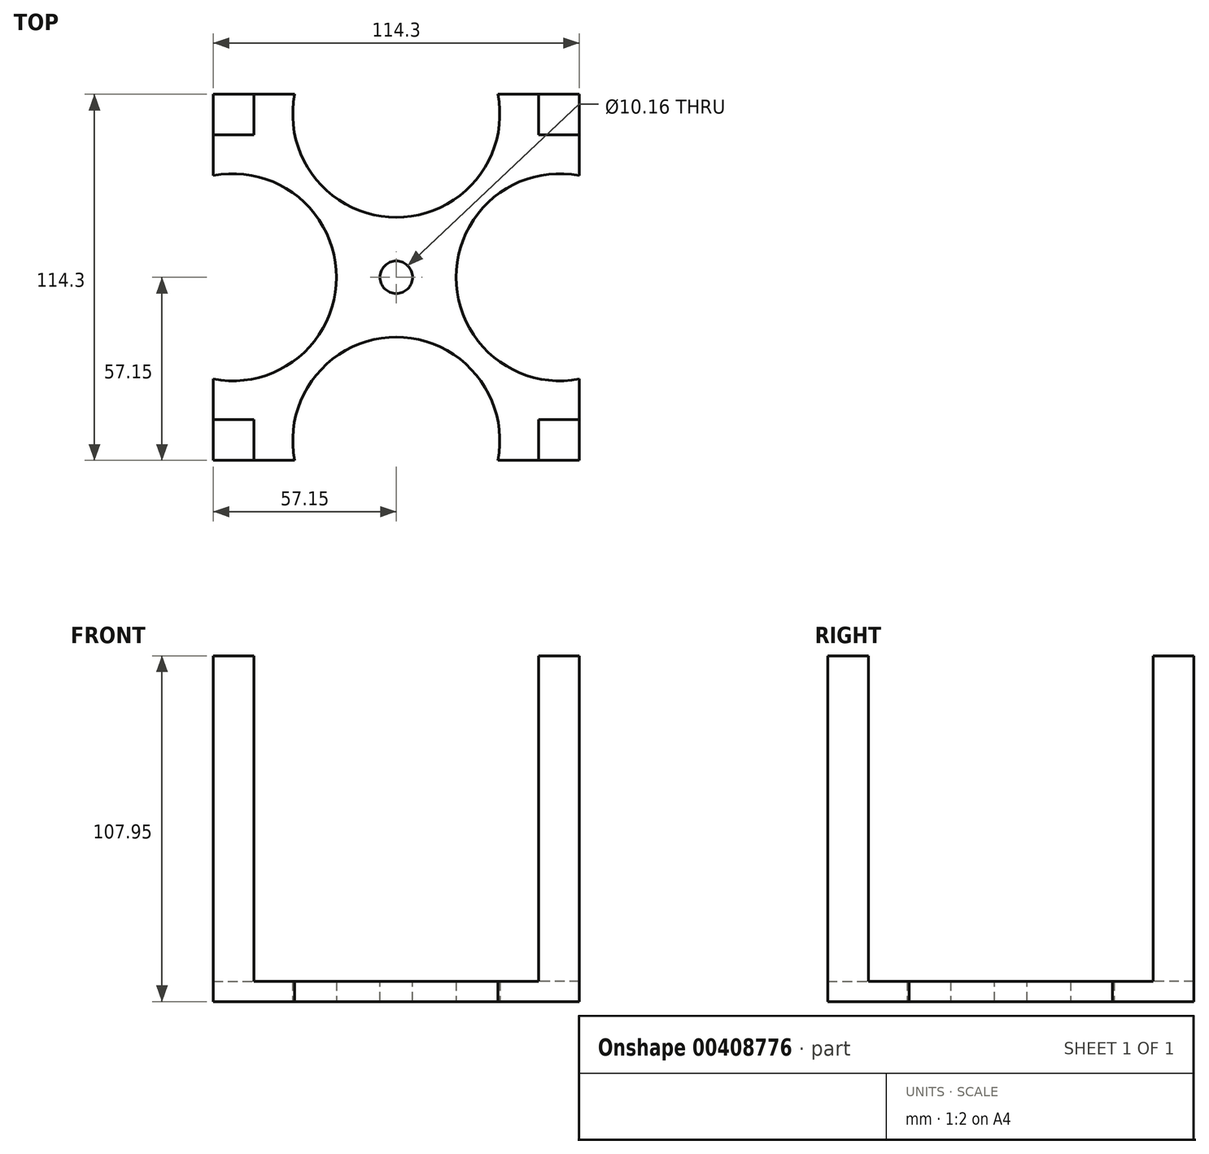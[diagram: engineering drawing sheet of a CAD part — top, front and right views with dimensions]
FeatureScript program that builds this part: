
annotation { "Feature Type Name" : "Feature", "Feature Type Description" : "" }
export const myFeature = defineFeature(function(context is Context, id is Id, definition is map)
    precondition{}
    {
        {
            var Q0;
            Q0=qCreatedBy(makeId("Top.planeOp"),FACE);
            var sketch = newSketch(context, id + "F0", { "sketchPlane" : qUnion([Q0])});
            skLineSegment(sketch, "E0.bottom", {"start": v(57.15, -57.15) * mm, "end": v(-57.15, -57.15) * mm});
            skLineSegment(sketch, "E0.top", {"start": v(57.15, 57.15) * mm, "end": v(-57.15, 57.15) * mm});
            skLineSegment(sketch, "E0.left", {"start": v(57.15, -57.15) * mm, "end": v(57.15, 57.15) * mm});
            skLineSegment(sketch, "E0.right", {"start": v(-57.15, -57.15) * mm, "end": v(-57.15, 57.15) * mm});
            skPoint(sketch, "E0.middle", {"position": v(0, 0) * mm});
            skSolve(sketch);
        }
        {
            var Q0;
            Q0 = qSketchRegion(id + "F0", true);
            extrude(context, id + "F1", {"entities" : qUnion([Q0]), "depth" : 6.35 * mm});
        }
        {
            var Q0;
            Q0=makeQuery(id+"F1.opExtrude","CAP_FACE",FACE,{"disambiguationData":[OSD([sQuery(id+"F0.wireOp",EDGE,"E0.bottom"),sQuery(id+"F0.wireOp",EDGE,"E0.top"),sQuery(id+"F0.wireOp",EDGE,"E0.left"),sQuery(id+"F0.wireOp",EDGE,"E0.right")])],"isStart":false});
            var sketch = newSketch(context, id + "F2", { "sketchPlane" : qUnion([Q0])});
            skLineSegment(sketch, "E1.bottom", {"start": v(57.15, 57.15) * mm, "end": v(44.45, 57.15) * mm});
            skLineSegment(sketch, "E1.top", {"start": v(57.15, 44.45) * mm, "end": v(44.45, 44.45) * mm});
            skLineSegment(sketch, "E1.left", {"start": v(57.15, 57.15) * mm, "end": v(57.15, 44.45) * mm});
            skLineSegment(sketch, "E1.right", {"start": v(44.45, 57.15) * mm, "end": v(44.45, 44.45) * mm});
            skLineSegment(sketch, "E2.1.0", {"start": v(-57.15, 44.45) * mm, "end": v(-44.45, 44.45) * mm});
            skLineSegment(sketch, "E2.1.1", {"start": v(-44.45, 57.15) * mm, "end": v(-44.45, 44.45) * mm});
            skLineSegment(sketch, "E2.1.2", {"start": v(-57.15, 57.15) * mm, "end": v(-44.45, 57.15) * mm});
            skLineSegment(sketch, "E2.1.3", {"start": v(-57.15, 57.15) * mm, "end": v(-57.15, 44.45) * mm});
            skLineSegment(sketch, "E2.2.0", {"start": v(-44.45, -57.15) * mm, "end": v(-44.45, -44.45) * mm});
            skLineSegment(sketch, "E2.2.1", {"start": v(-57.15, -44.45) * mm, "end": v(-44.45, -44.45) * mm});
            skLineSegment(sketch, "E2.2.2", {"start": v(-57.15, -57.15) * mm, "end": v(-57.15, -44.45) * mm});
            skLineSegment(sketch, "E2.2.3", {"start": v(-57.15, -57.15) * mm, "end": v(-44.45, -57.15) * mm});
            skLineSegment(sketch, "E2.3.0", {"start": v(57.15, -44.45) * mm, "end": v(44.45, -44.45) * mm});
            skLineSegment(sketch, "E2.3.1", {"start": v(44.45, -57.15) * mm, "end": v(44.45, -44.45) * mm});
            skLineSegment(sketch, "E2.3.2", {"start": v(57.15, -57.15) * mm, "end": v(44.45, -57.15) * mm});
            skLineSegment(sketch, "E2.3.3", {"start": v(57.15, -57.15) * mm, "end": v(57.15, -44.45) * mm});
            skPoint(sketch, "E2.center", {"position": v(0, 0) * mm});
            skSolve(sketch);
        }
        {
            var Q0;
            Q0=makeQuery(id+"F2.imprint","IMPRINT",FACE,{"disambiguationData":[TD([[makeQuery(id+"F2.imprint","IMPRINT",EDGE,{"derivedFrom":makeQuery(id+"F1.opExtrude","CAP_EDGE",EDGE,{"disambiguationData":[OSD([sQuery(id+"F0.wireOp",EDGE,"E0.bottom")])],"isStart":false})}),-1.0]])]});
            var sketch = newSketch(context, id + "F3", { "sketchPlane" : qUnion([Q0])});
            skCircle(sketch, "E3", {"center": v(0, 0) * mm, "radius": 5.08 * mm});
            skSolve(sketch);
        }
        {
            var Q0;
            Q0 = qSketchRegion(id + "F3", true);
            extrude(context, id + "F4", {"entities" : qUnion([Q0]), "operationType" : NewBodyOperationType.REMOVE, "oppositeDirection" : true, "depth" : 25.4 * mm});
        }
        {
            var Q0;
            Q0 = qSketchRegion(id + "F2", true);
            extrude(context, id + "F5", {"entities" : qUnion([Q0]), "operationType" : NewBodyOperationType.ADD, "depth" : 101.6 * mm});
        }
        {
            var Q0;
            Q0=makeQuery(id+"F1.opExtrude","CAP_FACE",FACE,{"disambiguationData":[OSD([sQuery(id+"F0.wireOp",EDGE,"E0.bottom"),sQuery(id+"F0.wireOp",EDGE,"E0.top"),sQuery(id+"F0.wireOp",EDGE,"E0.left"),sQuery(id+"F0.wireOp",EDGE,"E0.right")])],"isStart":true});
            var sketch = newSketch(context, id + "F6", { "sketchPlane" : qUnion([Q0])});
            skPoint(sketch, "E4.center", {"position": v(0, 0) * mm});
            skArc(sketch, "E5", {"start": v(-57.15, -31.75) * mm, "mid": v(-18.7, 0) * mm, "end": v(-57.15, 31.75) * mm});
            skArc(sketch, "E6.1.0", {"start": v(31.75, -57.15) * mm, "mid": v(0, -18.7) * mm, "end": v(-31.75, -57.15) * mm});
            skArc(sketch, "E6.2.0", {"start": v(57.15, 31.75) * mm, "mid": v(18.7, 0) * mm, "end": v(57.15, -31.75) * mm});
            skArc(sketch, "E6.3.0", {"start": v(-31.75, 57.15) * mm, "mid": v(0, 18.7) * mm, "end": v(31.75, 57.15) * mm});
            skLineSegment(sketch, "E7", {"start": v(-31.75, -57.15) * mm, "end": v(31.75, -57.15) * mm});
            skLineSegment(sketch, "E8", {"start": v(57.15, -31.75) * mm, "end": v(57.15, 31.75) * mm});
            skLineSegment(sketch, "E9", {"start": v(31.75, 57.15) * mm, "end": v(-31.75, 57.15) * mm});
            skLineSegment(sketch, "E10", {"start": v(-57.15, 31.75) * mm, "end": v(-57.15, -31.75) * mm});
            skSolve(sketch);
        }
        {
            var Q0;
            Q0 = qSketchRegion(id + "F6", true);
            extrude(context, id + "F7", {"entities" : qUnion([Q0]), "operationType" : NewBodyOperationType.REMOVE, "endBound" : BoundingType.THROUGH_ALL, "oppositeDirection" : true, "depth" : 25.4 * mm});
        }
    });
